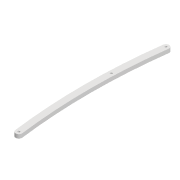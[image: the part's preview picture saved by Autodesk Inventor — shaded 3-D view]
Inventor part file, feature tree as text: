
AUTODESK INVENTOR PART (.ipt)
format: ipt  version: 2022 (Build 260153000, 153)  size: 97,792 bytes
history: native  units: mm
features: extrude x1
ambient origin geometry x8: Origin, YZ Plane, XZ Plane, XY Plane, X Axis, Y Axis, Z Axis, Center Point
bodies: Solid1 (feature_tree)
feature tree (1):
  extrude  "Extrusion1"  Depth=3.3mm
